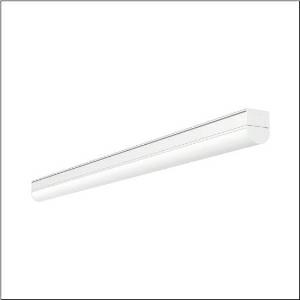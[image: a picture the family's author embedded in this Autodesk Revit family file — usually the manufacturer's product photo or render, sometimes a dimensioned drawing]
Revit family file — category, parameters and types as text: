
# Revit family: ecopack_r__31_51lj12mnm70a_41d1
name_source: partatom
category: Lighting Fixtures
units: mm (PartAtom-declared; Revit-internal decimal feet)

## family parameters
Cut with Voids When Loaded = No
Host = Face
Light Source = No
Part Type = Normal
Room Calculation Point = No
Round Connector Dimension = Use Diameter
Shared = No

## types (1)
- --- (1 x LED, 6780 lm, 50 W, 5000K)
    Apparent Load = 50 VA
    CIE Flux Codes = 39 67 87 89 100
    Color Rendering = 80
    Color Temperature = 5000K
    Default Elevation = 1800 mm
    Description = Ecopack® 31, diffuser luminaire, primary optical cover: cover, of PC, frosted, light emission: direct distribution, primary light characteristic: symmetric, installation type: surface-mounted, LED, rated luminous flux: 7.000lm, luminous efficacy: 140lm/W, light colour: 830/840/850, colour temperature: 3000/4000/5000K, control gear: ON/OFF Multilumen, with terminal, 3-pole, mains connection: 220..240V, AC, 50/60Hz, rated input power: 50W, housing, of aluminium, traffic white (RAL 9016), length: 1.450mm, width: 56mm, height: 68mm, end cap, of PC, white, protection rating (complete): IP20, insulation class (complete): insulation class I (protective earthing), certification: CE, impact resistance: IK06, permissible operating ambient temperature: -20..+40°C, packaging unit: 1 piece
    Height = 68 mm
    Lamp = 1 x LED
    Lamp Light Flux = 6780 lm
    Lamp Power = 50 W
    Lamp count = 1
    Length = 1450 mm
    Luminous efficacy = 136 lm/W
    Manufacturer = Siteco
    ModVariant = No
    Model = 51LJ12MNM70A
    Mounting Place = Ceiling
    Mounting Type = Surface mounted
    Number of Poles = 1
    OnlyDefault = Yes
    Power Factor = 1
    Product Name = Ecopack® 31
    Product group = diffuser luminaire
    ProductGroupID = 306
    Protection Class = Protection class I
    Protection Degree = IP 20
    RLX_Detail_Level = 1
    RLX_Emergency_Light_Flux = 0 lm
    RLX_Emergency_Type = 0
    RLX_Emergency_Type_DB = No
    RlxData = <blob elided: 38989 chars, md5=d5de1df7>
    Socket = socket
    Standby Power = 0 W
    System Light Flux = 6780 lm
    System Power = 50 W
    Type Comments = individual setting: colour temperature 5000K, luminous flux: 100 % | (ON | ON)
    Type Image = l_1007033.jpg
    URL = http://relux.com
    VarID = @adj_173974
    Voltage = 0 V
    Weight = 0.00 kg
    Width = 56 mm

## geometry (parser evidence)
native form markers: Blend x4, Sweep x14
no freeform markers — native parametric forms only
